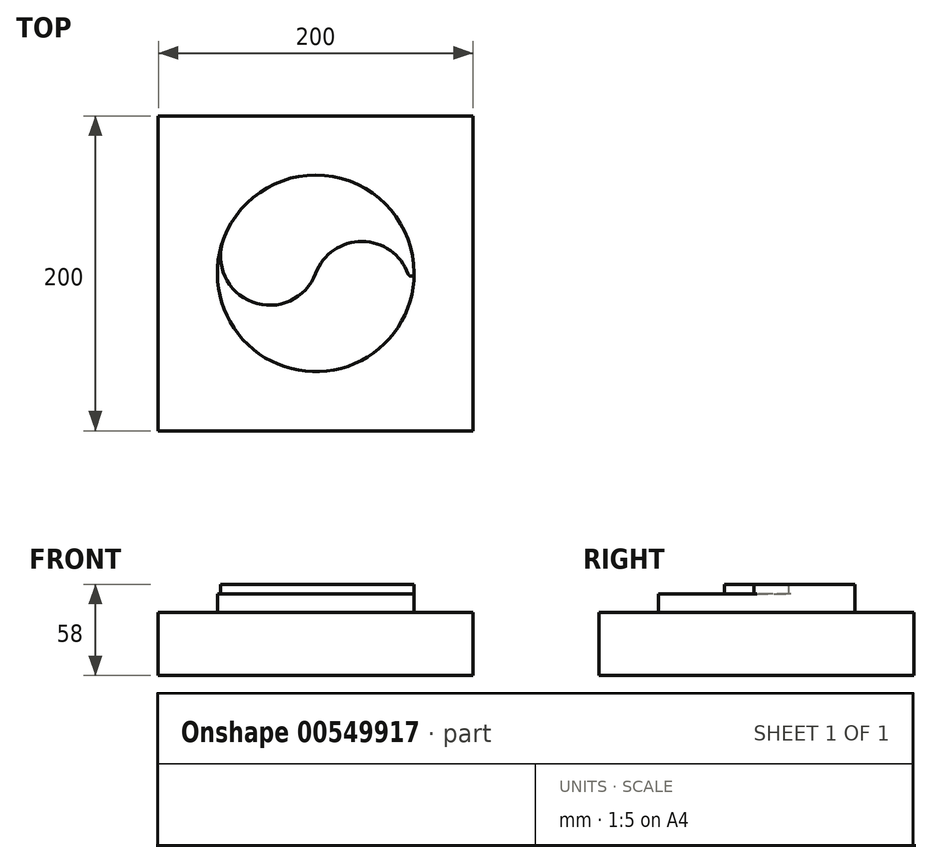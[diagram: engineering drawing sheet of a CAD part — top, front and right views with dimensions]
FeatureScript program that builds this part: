
annotation { "Feature Type Name" : "Feature", "Feature Type Description" : "" }
export const myFeature = defineFeature(function(context is Context, id is Id, definition is map)
    precondition{}
    {
        {
            var Q0;
            Q0=qCreatedBy(makeId("Top.planeOp"),FACE);
            var sketch = newSketch(context, id + "F0", { "sketchPlane" : qUnion([Q0])});
            skLineSegment(sketch, "E0.bottom", {"start": v(-102.3, 113.07) * mm, "end": v(97.7, 113.07) * mm});
            skLineSegment(sketch, "E0.top", {"start": v(-102.3, -86.93) * mm, "end": v(97.7, -86.93) * mm});
            skLineSegment(sketch, "E0.left", {"start": v(-102.3, 113.07) * mm, "end": v(-102.3, -86.93) * mm});
            skLineSegment(sketch, "E0.right", {"start": v(97.7, 113.07) * mm, "end": v(97.7, -86.93) * mm});
            skSolve(sketch);
        }
        {
            var Q0;
            Q0=makeQuery(id+"F0.imprint","IMPRINT",FACE,{"disambiguationData":[TD([[makeQuery(id+"F0.imprint","IMPRINT",EDGE,{"derivedFrom":sQuery(id+"F0.wireOp",EDGE,"E0.bottom")}),-1.0]])]});
            extrude(context, id + "F1", {"entities" : qUnion([Q0]), "depth" : 40 * mm, "offsetDistance" : 25 * mm});
        }
        {
            var Q0;
            Q0=makeQuery(id+"F1.opExtrude","CAP_FACE",FACE,{"disambiguationData":[OSD([sQuery(id+"F0.wireOp",EDGE,"E0.bottom"),sQuery(id+"F0.wireOp",EDGE,"E0.top"),sQuery(id+"F0.wireOp",EDGE,"E0.left"),sQuery(id+"F0.wireOp",EDGE,"E0.right")])],"isStart":false});
            var sketch = newSketch(context, id + "F2", { "sketchPlane" : qUnion([Q0])});
            skCircle(sketch, "E1", {"center": v(-2.3, 13.07) * mm, "radius": 62.49 * mm});
            skLineSegment(sketch, "E2", {"start": v(-102.3, 13.07) * mm, "end": v(97.7, 13.07) * mm});
            skPoint(sketch, "E3", {"position": v(-64.78, 13.07) * mm});
            skPoint(sketch, "E4", {"position": v(60.2, 13.07) * mm});
            skPoint(sketch, "E5", {"position": v(-60.81, 34.99) * mm});
            skPoint(sketch, "E6", {"position": v(56.23, -8.84) * mm});
            skPoint(sketch, "E7", {"position": v(26.97, 2.12) * mm});
            skArc(sketch, "E8", {"start": v(-60.81, 34.99) * mm, "mid": v(-42.51, -5.23) * mm, "end": v(-2.3, 13.07) * mm});
            skArc(sketch, "E9", {"start": v(56.23, -8.84) * mm, "mid": v(37.93, 31.38) * mm, "end": v(-2.3, 13.07) * mm});
            skSolve(sketch);
        }
        {
            var Q0;
            {var subQ1=sQuery(id+"F2.wireOp",EDGE,"E1");var subQ5=sQuery(id+"F2.wireOp",EDGE,"E8");var subQ8=makeQuery(id+"F2.imprint","INTERSECT",VERTEX,{"derivedFrom":[subQ1,subQ5]});Q0=makeQuery(id+"F2.imprint","IMPRINT",FACE,{"disambiguationData":[TD([[makeQuery(id+"F2.imprint","IMPRINT",EDGE,{"disambiguationData":[TD([[subQ8,1.0]])],"derivedFrom":subQ1}),1.0]])]});}
            var Q1;
            {var subQ0=sQuery(id+"F2.wireOp",EDGE,"E8");var subQ1=sQuery(id+"F2.wireOp",EDGE,"E2");var subQ3=makeQuery(id+"F2.imprint","INTERSECT",VERTEX,{"derivedFrom":[subQ1,subQ0]});Q1=makeQuery(id+"F2.imprint","IMPRINT",FACE,{"disambiguationData":[TD([[makeQuery(id+"F2.imprint","IMPRINT",EDGE,{"disambiguationData":[TD([[subQ3,-1.0]])],"derivedFrom":subQ1}),-1.0]])]});}
            var Q2;
            {var subQ0=sQuery(id+"F2.wireOp",EDGE,"E9");var subQ5=sQuery(id+"F2.wireOp",EDGE,"E1");var subQ8=makeQuery(id+"F2.imprint","INTERSECT",VERTEX,{"derivedFrom":[subQ5,subQ0]});Q2=makeQuery(id+"F2.imprint","IMPRINT",FACE,{"disambiguationData":[TD([[makeQuery(id+"F2.imprint","IMPRINT",EDGE,{"disambiguationData":[TD([[subQ8,1.0]])],"derivedFrom":subQ5}),1.0]])]});}
            var Q3;
            {var subQ0=sQuery(id+"F2.wireOp",EDGE,"E8");var subQ1=sQuery(id+"F2.wireOp",EDGE,"E1");var subQ2=makeQuery(id+"F2.imprint","INTERSECT",VERTEX,{"derivedFrom":[subQ1,subQ0]});Q3=makeQuery(id+"F2.imprint","IMPRINT",FACE,{"disambiguationData":[TD([[makeQuery(id+"F2.imprint","IMPRINT",EDGE,{"disambiguationData":[TD([[subQ2,-1.0]])],"derivedFrom":subQ1}),1.0]])]});}
            var Q4;
            {var subQ0=sQuery(id+"F2.wireOp",EDGE,"E9");var subQ1=sQuery(id+"F2.wireOp",EDGE,"E2");var subQ3=makeQuery(id+"F2.imprint","INTERSECT",VERTEX,{"derivedFrom":[subQ1,subQ0]});Q4=makeQuery(id+"F2.imprint","IMPRINT",FACE,{"disambiguationData":[TD([[makeQuery(id+"F2.imprint","IMPRINT",EDGE,{"disambiguationData":[TD([[subQ3,1.0]])],"derivedFrom":subQ1}),1.0]])]});}
            var Q5;
            {var subQ0=sQuery(id+"F2.wireOp",EDGE,"E9");var subQ1=sQuery(id+"F2.wireOp",EDGE,"E1");var subQ2=makeQuery(id+"F2.imprint","INTERSECT",VERTEX,{"derivedFrom":[subQ1,subQ0]});Q5=makeQuery(id+"F2.imprint","IMPRINT",FACE,{"disambiguationData":[TD([[makeQuery(id+"F2.imprint","IMPRINT",EDGE,{"disambiguationData":[TD([[subQ2,-1.0]])],"derivedFrom":subQ1}),1.0]])]});}
            extrude(context, id + "F3", {"entities" : qUnion([Q0, Q1, Q2, Q3, Q4, Q5]), "operationType" : NewBodyOperationType.ADD, "depth" : 12 * mm, "offsetDistance" : 25 * mm});
        }
        {
            var Q0;
            {var subQ1=sQuery(id+"F2.wireOp",EDGE,"E1");var subQ5=sQuery(id+"F2.wireOp",EDGE,"E8");var subQ8=makeQuery(id+"F2.imprint","INTERSECT",VERTEX,{"derivedFrom":[subQ1,subQ5]});Q0=makeQuery(id+"F2.imprint","IMPRINT",FACE,{"disambiguationData":[TD([[makeQuery(id+"F2.imprint","IMPRINT",EDGE,{"disambiguationData":[TD([[subQ8,1.0]])],"derivedFrom":subQ1}),1.0]])]});}
            var Q1;
            {var subQ0=sQuery(id+"F2.wireOp",EDGE,"E8");var subQ1=sQuery(id+"F2.wireOp",EDGE,"E2");var subQ3=makeQuery(id+"F2.imprint","INTERSECT",VERTEX,{"derivedFrom":[subQ1,subQ0]});Q1=makeQuery(id+"F2.imprint","IMPRINT",FACE,{"disambiguationData":[TD([[makeQuery(id+"F2.imprint","IMPRINT",EDGE,{"disambiguationData":[TD([[subQ3,-1.0]])],"derivedFrom":subQ1}),-1.0]])]});}
            var Q2;
            {var subQ0=sQuery(id+"F2.wireOp",EDGE,"E9");var subQ1=sQuery(id+"F2.wireOp",EDGE,"E1");var subQ2=makeQuery(id+"F2.imprint","INTERSECT",VERTEX,{"derivedFrom":[subQ1,subQ0]});Q2=makeQuery(id+"F2.imprint","IMPRINT",FACE,{"disambiguationData":[TD([[makeQuery(id+"F2.imprint","IMPRINT",EDGE,{"disambiguationData":[TD([[subQ2,-1.0]])],"derivedFrom":subQ1}),1.0]])]});}
            extrude(context, id + "F4", {"entities" : qUnion([Q0, Q1, Q2]), "operationType" : NewBodyOperationType.ADD, "depth" : 18 * mm, "offsetDistance" : 25 * mm});
        }
        {
            var Q0;
            Q0=makeQuery(id+"F4.opExtrude","SWEPT_EDGE",EDGE,{"disambiguationData":[OSD([sQuery(id+"F2.wireOp",EDGE,"E1"),sQuery(id+"F2.wireOp",EDGE,"E9")])]});
            fillet(context, id + "F5", {"entities" : qUnion([Q0]), "radius" : 1.96 * mm, "tangentPropagation" : true, "allowEdgeOverflow" : false});
        }
    });
